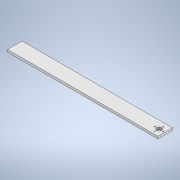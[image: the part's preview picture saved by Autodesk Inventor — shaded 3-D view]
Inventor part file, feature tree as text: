
AUTODESK INVENTOR PART (.ipt)
format: ipt  version: 2022 (Build 260153000, 153)  size: 130,048 bytes
history: native  units: mm
features: sketch x3, hole x2, other x1, extrude x1
ambient origin geometry x8: Origin, YZ Plane, XZ Plane, XY Plane, X Axis, Y Axis, Z Axis, Center Point
bodies: Body1 (feature_tree)
feature tree (7):
  other  "ソリッド1"
  extrude  "押し出し1"  Depth=30.0mm
  hole  "穴1"  [1 undecoded]
  hole  "穴2"  [1 undecoded]
  sketch  "スケッチ1"
  sketch  "スケッチ2"
  sketch  "スケッチ3"
note: 2 required parameter values undecoded (feature->parameter linkage not recoverable at this tier; creation-order binding heuristic only, values carry confidence <= 0.55)
